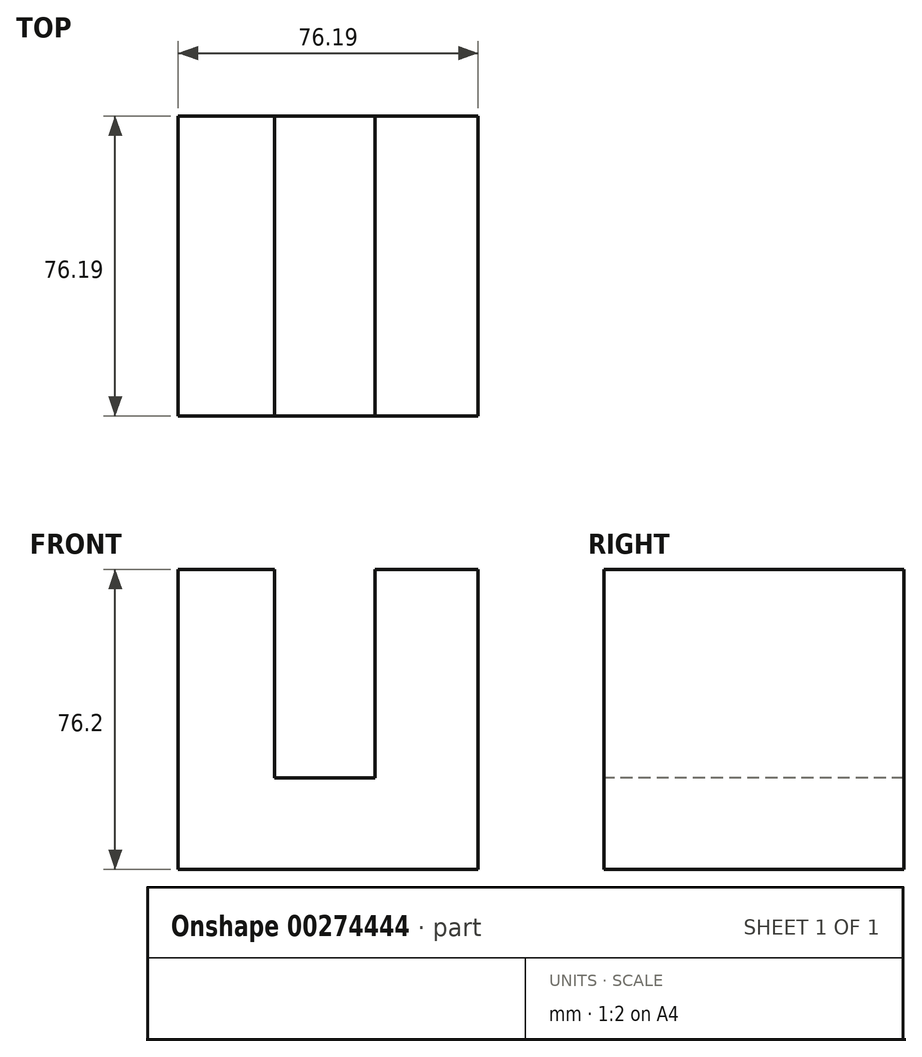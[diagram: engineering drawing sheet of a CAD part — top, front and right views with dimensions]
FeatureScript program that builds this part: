
annotation { "Feature Type Name" : "Feature", "Feature Type Description" : "" }
export const myFeature = defineFeature(function(context is Context, id is Id, definition is map)
    precondition{}
    {
        {
            var Q0;
            Q0=qCreatedBy(makeId("Top.planeOp"),FACE);
            var sketch = newSketch(context, id + "F0", { "sketchPlane" : qUnion([Q0])});
            skLineSegment(sketch, "E0.bottom", {"start": v(0, 0) * mm, "end": v(-76.2, 0) * mm});
            skLineSegment(sketch, "E0.top", {"start": v(0, 76.2) * mm, "end": v(-76.2, 76.2) * mm});
            skLineSegment(sketch, "E0.left", {"start": v(0, 0) * mm, "end": v(0, 76.2) * mm});
            skLineSegment(sketch, "E0.right", {"start": v(-76.2, 0) * mm, "end": v(-76.2, 76.2) * mm});
            skSolve(sketch);
        }
        {
            var Q0;
            Q0 = qSketchRegion(id + "F0", true);
            extrude(context, id + "F1", {"entities" : qUnion([Q0]), "depth" : 76.2 * mm});
        }
        {
            var Q0;
            Q0=makeQuery(id+"F1.opExtrude","SWEPT_FACE",FACE,{"disambiguationData":[OSD([sQuery(id+"F0.wireOp",EDGE,"E0.bottom")])]});
            var sketch = newSketch(context, id + "F2", { "sketchPlane" : qUnion([Q0])});
            skLineSegment(sketch, "E1.bottom", {"start": v(-51.75, 76.2) * mm, "end": v(-26.16, 76.2) * mm});
            skLineSegment(sketch, "E1.top", {"start": v(-51.75, 23.3) * mm, "end": v(-26.16, 23.3) * mm});
            skLineSegment(sketch, "E1.left", {"start": v(-51.75, 76.2) * mm, "end": v(-51.75, 23.3) * mm});
            skLineSegment(sketch, "E1.right", {"start": v(-26.16, 76.2) * mm, "end": v(-26.16, 23.3) * mm});
            skSolve(sketch);
        }
        {
            var Q0;
            Q0 = qSketchRegion(id + "F2", true);
            extrude(context, id + "F3", {"entities" : qUnion([Q0]), "operationType" : NewBodyOperationType.REMOVE, "oppositeDirection" : true, "depth" : 76.2 * mm});
        }
    });
